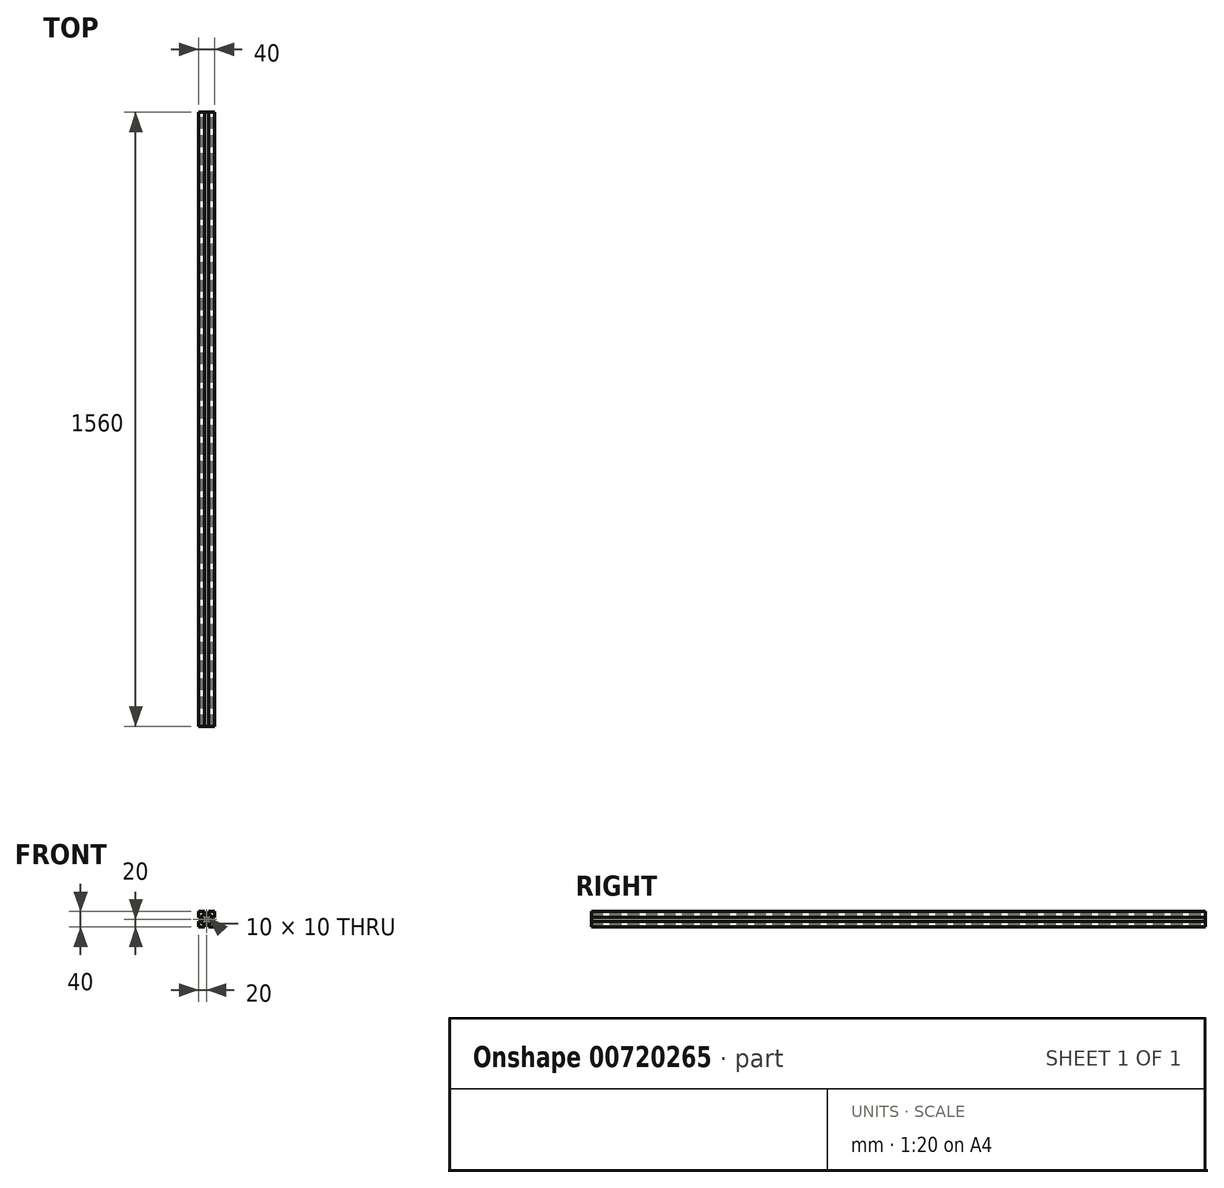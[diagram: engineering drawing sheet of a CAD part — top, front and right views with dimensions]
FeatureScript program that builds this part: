
annotation { "Feature Type Name" : "Feature", "Feature Type Description" : "" }
export const myFeature = defineFeature(function(context is Context, id is Id, definition is map)
    precondition{}
    {
        {
            var Q0;
            Q0=qCreatedBy(makeId("Front.planeOp"),FACE);
            var sketch = newSketch(context, id + "F0", { "sketchPlane" : qUnion([Q0])});
            skLineSegment(sketch, "E0.bottom", {"start": v(20, 20) * mm, "end": v(5, 20) * mm});
            skLineSegment(sketch, "E0.top", {"start": v(20, -20) * mm, "end": v(5, -20) * mm});
            skLineSegment(sketch, "E0.left", {"start": v(20, 20) * mm, "end": v(20, 5) * mm});
            skLineSegment(sketch, "E0.right", {"start": v(-20, 20) * mm, "end": v(-20, 5) * mm});
            skPoint(sketch, "E0.middle", {"position": v(0, 0) * mm});
            skLineSegment(sketch, "E1", {"start": v(0, 20) * mm, "end": v(0, -20) * mm, "construction": true});
            skLineSegment(sketch, "E2", {"start": v(-20, 0) * mm, "end": v(20, 0) * mm, "construction": true});
            skLineSegment(sketch, "E3", {"start": v(-20, 5) * mm, "end": v(-15, 5) * mm});
            skLineSegment(sketch, "E4", {"start": v(-20, -5) * mm, "end": v(-15, -5) * mm});
            skLineSegment(sketch, "E5", {"start": v(-5, 20) * mm, "end": v(-5, 15) * mm});
            skLineSegment(sketch, "E6", {"start": v(5, 20) * mm, "end": v(5, 15) * mm});
            skLineSegment(sketch, "E7", {"start": v(-10, 15) * mm, "end": v(-5, 15) * mm});
            skLineSegment(sketch, "E8", {"start": v(-10, -15) * mm, "end": v(-5, -15) * mm});
            skLineSegment(sketch, "E9", {"start": v(15, 10) * mm, "end": v(15, 5) * mm});
            skLineSegment(sketch, "E10", {"start": v(-15, 10) * mm, "end": v(-10, 5) * mm});
            skLineSegment(sketch, "E11", {"start": v(-10, 15) * mm, "end": v(-5, 10) * mm});
            skLineSegment(sketch, "E12", {"start": v(-15, -10) * mm, "end": v(-10, -5) * mm});
            skLineSegment(sketch, "E13", {"start": v(-10, -15) * mm, "end": v(-5, -10) * mm});
            skLineSegment(sketch, "E14.trimOffspring", {"start": v(20, -5) * mm, "end": v(20, -20) * mm});
            skLineSegment(sketch, "E15.trimOffspring", {"start": v(-20, -5) * mm, "end": v(-20, -20) * mm});
            skLineSegment(sketch, "E16.trimOffspring", {"start": v(-5, -20) * mm, "end": v(-20, -20) * mm});
            skLineSegment(sketch, "E17.trimOffspring", {"start": v(-5, 20) * mm, "end": v(-20, 20) * mm});
            skLineSegment(sketch, "E18.trimOffspring", {"start": v(5, 15) * mm, "end": v(10, 15) * mm});
            skLineSegment(sketch, "E19.trimOffspring", {"start": v(-15, -5) * mm, "end": v(-15, -10) * mm});
            skLineSegment(sketch, "E20.trimOffspring", {"start": v(15, -5) * mm, "end": v(15, -10) * mm});
            skLineSegment(sketch, "E21.trimOffspring", {"start": v(5, -15) * mm, "end": v(10, -15) * mm});
            skLineSegment(sketch, "E22.trimOffspring", {"start": v(-5, 5) * mm, "end": v(-5, -5) * mm});
            skLineSegment(sketch, "E23.trimOffspring", {"start": v(5, 5) * mm, "end": v(5, -5) * mm});
            skLineSegment(sketch, "E24.trimOffspring", {"start": v(15, 5) * mm, "end": v(20, 5) * mm});
            skLineSegment(sketch, "E25.trimOffspring", {"start": v(15, -5) * mm, "end": v(20, -5) * mm});
            skLineSegment(sketch, "E26.trimOffspring", {"start": v(5, -15) * mm, "end": v(5, -20) * mm});
            skLineSegment(sketch, "E27.trimOffspring", {"start": v(-5, -15) * mm, "end": v(-5, -20) * mm});
            skLineSegment(sketch, "E28.trimOffspring", {"start": v(-5, -5) * mm, "end": v(5, -5) * mm});
            skLineSegment(sketch, "E29.trimOffspring", {"start": v(-5, 5) * mm, "end": v(5, 5) * mm});
            skLineSegment(sketch, "E30", {"start": v(10, 5) * mm, "end": v(10, -5) * mm});
            skLineSegment(sketch, "E31", {"start": v(-5, 10) * mm, "end": v(5, 10) * mm});
            skLineSegment(sketch, "E32", {"start": v(-10, 5) * mm, "end": v(-10, -5) * mm});
            skLineSegment(sketch, "E33", {"start": v(-5, -10) * mm, "end": v(5, -10) * mm});
            skLineSegment(sketch, "E34.trimOffspring", {"start": v(-15, 10) * mm, "end": v(-15, 5) * mm});
            skPoint(sketch, "E35.orphan", {"position": v(20, 15) * mm});
            skPoint(sketch, "E36.orphan", {"position": v(20, -15) * mm});
            skPoint(sketch, "E37.orphan", {"position": v(15, -20) * mm});
            skPoint(sketch, "E38.orphan", {"position": v(-15, -20) * mm});
            skLineSegment(sketch, "E39.trimOffspring", {"start": v(-5, 0) * mm, "end": v(0, -5) * mm});
            skLineSegment(sketch, "E40.trimOffspring", {"start": v(-5, 0) * mm, "end": v(0, 5) * mm});
            skLineSegment(sketch, "E41.trimOffspring", {"start": v(0, 5) * mm, "end": v(5, 0) * mm});
            skLineSegment(sketch, "E42.trimOffspring", {"start": v(5, 10) * mm, "end": v(10, 15) * mm});
            skLineSegment(sketch, "E43.trimOffspring", {"start": v(10, 5) * mm, "end": v(15, 10) * mm});
            skLineSegment(sketch, "E44.trimOffspring", {"start": v(10, -5) * mm, "end": v(15, -10) * mm});
            skLineSegment(sketch, "E45.trimOffspring", {"start": v(5, -10) * mm, "end": v(10, -15) * mm});
            skLineSegment(sketch, "E46.trimOffspring", {"start": v(0, -5) * mm, "end": v(5, 0) * mm});
            skSolve(sketch);
        }
        {
            var Q0;
            Q0=makeQuery(id+"F0.imprint","IMPRINT",FACE,{"disambiguationData":[TD([[makeQuery(id+"F0.imprint","IMPRINT",EDGE,{"derivedFrom":sQuery(id+"F0.wireOp",EDGE,"E0.bottom")}),1.0]])]});
            extrude(context, id + "F1", {"entities" : qUnion([Q0]), "depth" : 1560 * mm, "offsetDistance" : 25 * mm});
        }
    });
